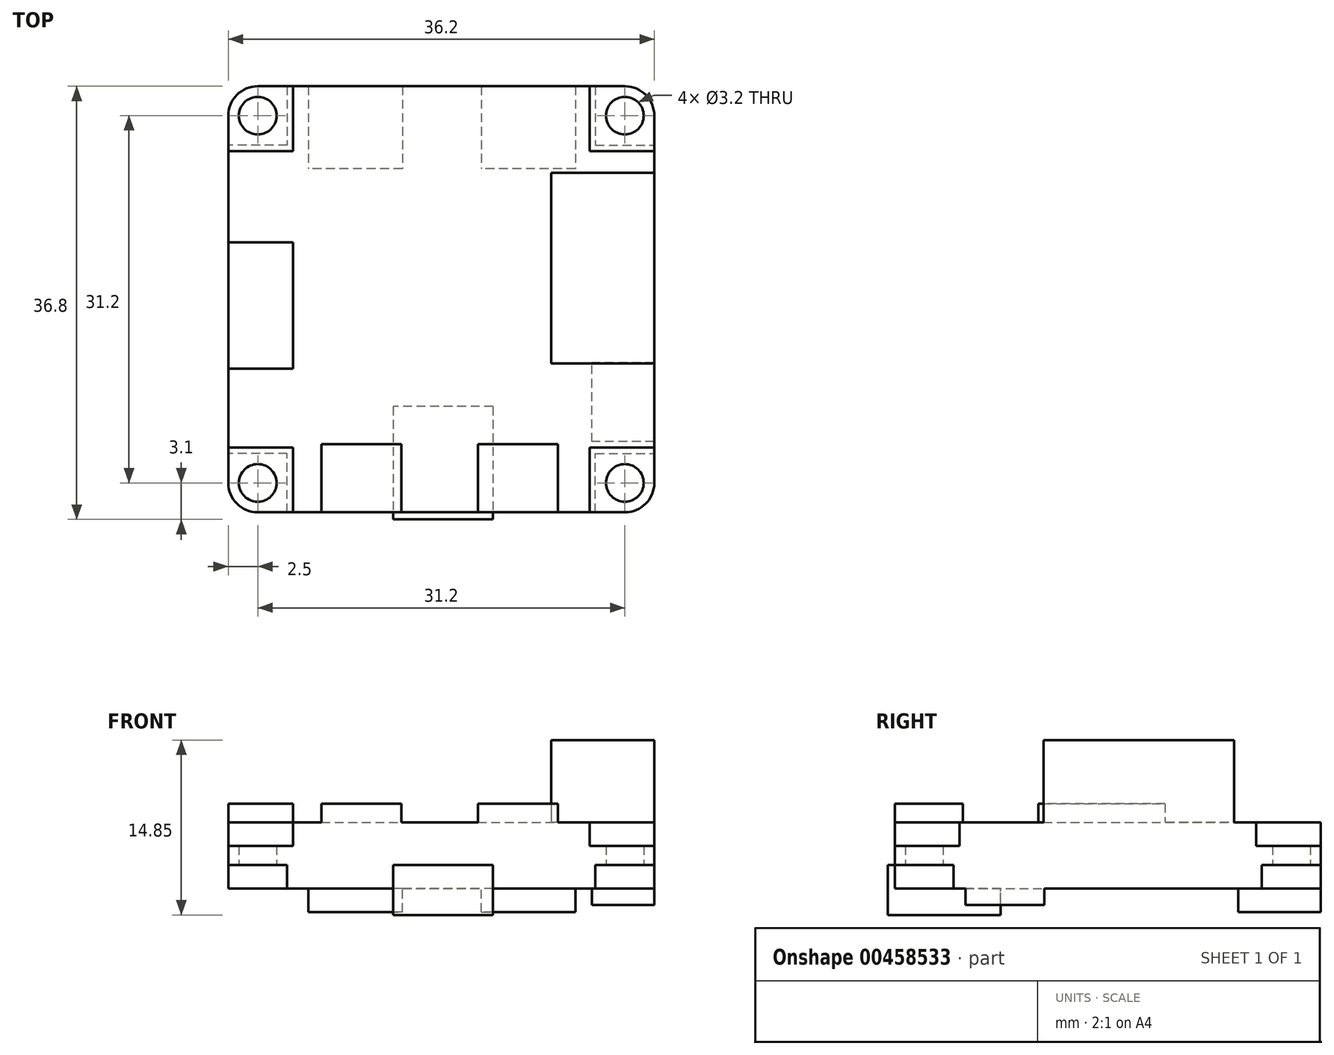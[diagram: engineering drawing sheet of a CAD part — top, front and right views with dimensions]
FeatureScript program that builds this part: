
annotation { "Feature Type Name" : "Feature", "Feature Type Description" : "" }
export const myFeature = defineFeature(function(context is Context, id is Id, definition is map)
    precondition{}
    {
        {
            var Q0;
            Q0=qCreatedBy(makeId("Top.planeOp"),FACE);
            var sketch = newSketch(context, id + "F0", { "sketchPlane" : qUnion([Q0])});
            skLineSegment(sketch, "E0.bottom", {"start": v(-15.6, 18.1) * mm, "end": v(15.6, 18.1) * mm});
            skLineSegment(sketch, "E0.top", {"start": v(-15.6, -18.1) * mm, "end": v(15.6, -18.1) * mm});
            skLineSegment(sketch, "E0.left", {"start": v(-18.1, 15.6) * mm, "end": v(-18.1, -15.6) * mm});
            skLineSegment(sketch, "E0.right", {"start": v(18.1, 15.6) * mm, "end": v(18.1, -15.6) * mm});
            skPoint(sketch, "E0.middle", {"position": v(0, 0) * mm});
            skPoint(sketch, "E1.visualSharp", {"position": v(-18.1, 18.1) * mm});
            skArc(sketch, "E1.filletArc", {"start": v(-15.6, 18.1) * mm, "mid": v(-17.37, 17.37) * mm, "end": v(-18.1, 15.6) * mm});
            skPoint(sketch, "E2.visualSharp", {"position": v(18.1, 18.1) * mm});
            skArc(sketch, "E2.filletArc", {"start": v(18.1, 15.6) * mm, "mid": v(17.37, 17.37) * mm, "end": v(15.6, 18.1) * mm});
            skPoint(sketch, "E3.visualSharp", {"position": v(18.1, -18.1) * mm});
            skArc(sketch, "E3.filletArc", {"start": v(15.6, -18.1) * mm, "mid": v(17.37, -17.37) * mm, "end": v(18.1, -15.6) * mm});
            skPoint(sketch, "E4.visualSharp", {"position": v(-18.1, -18.1) * mm});
            skArc(sketch, "E4.filletArc", {"start": v(-18.1, -15.6) * mm, "mid": v(-17.37, -17.37) * mm, "end": v(-15.6, -18.1) * mm});
            skCircle(sketch, "E5", {"center": v(-15.6, 15.6) * mm, "radius": 1.6 * mm});
            skCircle(sketch, "E6.MirrorC", {"center": v(15.6, 15.6) * mm, "radius": 1.6 * mm});
            skCircle(sketch, "E7.MirrorC", {"center": v(15.6, -15.6) * mm, "radius": 1.6 * mm});
            skCircle(sketch, "E8.MirrorC", {"center": v(-15.6, -15.6) * mm, "radius": 1.6 * mm});
            skSolve(sketch);
        }
        {
            var Q0;
            Q0=qSketchRegion(id+"F0",true);
            extrude(context, id + "F1", {"entities" : qUnion([Q0]), "depth" : 1.6 * mm});
        }
        {
            var Q0;
            Q0=makeQuery(id+"F1.opExtrude","CAP_FACE",FACE,{"disambiguationData":[OSD([sQuery(id+"F0.wireOp",EDGE,"E0.bottom"),sQuery(id+"F0.wireOp",EDGE,"E0.top"),sQuery(id+"F0.wireOp",EDGE,"E0.left"),sQuery(id+"F0.wireOp",EDGE,"E0.right"),sQuery(id+"F0.wireOp",EDGE,"E1.filletArc"),sQuery(id+"F0.wireOp",EDGE,"E2.filletArc"),sQuery(id+"F0.wireOp",EDGE,"E3.filletArc"),sQuery(id+"F0.wireOp",EDGE,"E4.filletArc"),sQuery(id+"F0.wireOp",EDGE,"E5"),sQuery(id+"F0.wireOp",EDGE,"E6.MirrorC"),sQuery(id+"F0.wireOp",EDGE,"E7.MirrorC"),sQuery(id+"F0.wireOp",EDGE,"E8.MirrorC")])],"isStart":false});
            var sketch = newSketch(context, id + "F2", { "sketchPlane" : qUnion([Q0])});
            skLineSegment(sketch, "E9.bottom", {"start": v(-18.1, -5.9) * mm, "end": v(-12.6, -5.9) * mm});
            skLineSegment(sketch, "E9.top", {"start": v(-18.1, 4.85) * mm, "end": v(-12.6, 4.85) * mm});
            skLineSegment(sketch, "E9.left", {"start": v(-18.1, -5.9) * mm, "end": v(-18.1, 4.85) * mm});
            skLineSegment(sketch, "E9.right", {"start": v(-12.6, -5.9) * mm, "end": v(-12.6, 4.85) * mm});
            skLineSegment(sketch, "E10.bottom", {"start": v(-10.2, -18.1) * mm, "end": v(-3.4, -18.1) * mm});
            skLineSegment(sketch, "E10.top", {"start": v(-10.2, -12.3) * mm, "end": v(-3.4, -12.3) * mm});
            skLineSegment(sketch, "E10.left", {"start": v(-10.2, -18.1) * mm, "end": v(-10.2, -12.3) * mm});
            skLineSegment(sketch, "E10.right", {"start": v(-3.4, -18.1) * mm, "end": v(-3.4, -12.3) * mm});
            skLineSegment(sketch, "E11.bottom", {"start": v(3.1, -18.1) * mm, "end": v(9.9, -18.1) * mm});
            skLineSegment(sketch, "E11.top", {"start": v(3.1, -12.3) * mm, "end": v(9.9, -12.3) * mm});
            skLineSegment(sketch, "E11.left", {"start": v(3.1, -18.1) * mm, "end": v(3.1, -12.3) * mm});
            skLineSegment(sketch, "E11.right", {"start": v(9.9, -18.1) * mm, "end": v(9.9, -12.3) * mm});
            skLineSegment(sketch, "E12.bottom", {"start": v(18.1, -5.46) * mm, "end": v(9.35, -5.46) * mm});
            skLineSegment(sketch, "E12.top", {"start": v(18.1, 10.74) * mm, "end": v(9.35, 10.74) * mm});
            skLineSegment(sketch, "E12.left", {"start": v(18.1, -5.46) * mm, "end": v(18.1, 10.74) * mm});
            skLineSegment(sketch, "E12.right", {"start": v(9.35, -5.46) * mm, "end": v(9.35, 10.74) * mm});
            skLineSegment(sketch, "E13", {"start": v(-18.1, -12.6) * mm, "end": v(-12.6, -12.6) * mm});
            skLineSegment(sketch, "E14", {"start": v(-12.6, -12.6) * mm, "end": v(-12.6, -18.1) * mm});
            skLineSegment(sketch, "E15.MirrorCS", {"start": v(-18.1, 12.6) * mm, "end": v(-12.6, 12.6) * mm});
            skLineSegment(sketch, "E16.MirrorCS", {"start": v(-12.6, 12.6) * mm, "end": v(-12.6, 18.1) * mm});
            skLineSegment(sketch, "E17.MirrorCS", {"start": v(12.6, 12.6) * mm, "end": v(12.6, 18.1) * mm});
            skLineSegment(sketch, "E18.MirrorCS", {"start": v(18.1, 12.6) * mm, "end": v(12.6, 12.6) * mm});
            skLineSegment(sketch, "E19.MirrorCS", {"start": v(12.6, -12.6) * mm, "end": v(12.6, -18.1) * mm});
            skLineSegment(sketch, "E20.MirrorCS", {"start": v(18.1, -12.6) * mm, "end": v(12.6, -12.6) * mm});
            skSolve(sketch);
        }
        {
            var Q0;
            Q0=makeQuery(id+"F2.imprint","IMPRINT",FACE,{"disambiguationData":[TD([[makeQuery(id+"F2.imprint","IMPRINT",EDGE,{"derivedFrom":sQuery(id+"F2.wireOp",EDGE,"E9.bottom")}),1.0]])]});
            var Q1;
            Q1=makeQuery(id+"F2.imprint","IMPRINT",FACE,{"disambiguationData":[TD([[makeQuery(id+"F2.imprint","IMPRINT",EDGE,{"derivedFrom":sQuery(id+"F2.wireOp",EDGE,"E10.bottom")}),1.0]])]});
            var Q2;
            Q2=makeQuery(id+"F2.imprint","IMPRINT",FACE,{"disambiguationData":[TD([[makeQuery(id+"F2.imprint","IMPRINT",EDGE,{"derivedFrom":sQuery(id+"F2.wireOp",EDGE,"E11.bottom")}),1.0]])]});
            extrude(context, id + "F3", {"entities" : qUnion([Q0, Q1, Q2]), "operationType" : NewBodyOperationType.ADD, "depth" : 3.6 * mm});
        }
        {
            var Q0;
            Q0=makeQuery(id+"F2.imprint","IMPRINT",FACE,{"disambiguationData":[TD([[makeQuery(id+"F2.imprint","IMPRINT",EDGE,{"derivedFrom":sQuery(id+"F2.wireOp",EDGE,"E12.bottom")}),-1.0]])]});
            extrude(context, id + "F4", {"entities" : qUnion([Q0]), "operationType" : NewBodyOperationType.ADD, "depth" : 9 * mm});
        }
        {
            var Q0;
            {var subQ14=sQuery(id+"F2.wireOp",EDGE,"E9.bottom");Q0=makeQuery(id+"F2.imprint","IMPRINT",FACE,{"disambiguationData":[TD([[makeQuery(id+"F2.imprint","IMPRINT",EDGE,{"derivedFrom":subQ14}),-1.0]])]});}
            extrude(context, id + "F5", {"entities" : qUnion([Q0]), "operationType" : NewBodyOperationType.ADD, "depth" : 2 * mm});
        }
        {
            var Q0;
            Q0=makeQuery(id+"F1.opExtrude","CAP_FACE",FACE,{"disambiguationData":[OSD([sQuery(id+"F0.wireOp",EDGE,"E0.bottom"),sQuery(id+"F0.wireOp",EDGE,"E0.top"),sQuery(id+"F0.wireOp",EDGE,"E0.left"),sQuery(id+"F0.wireOp",EDGE,"E0.right"),sQuery(id+"F0.wireOp",EDGE,"E1.filletArc"),sQuery(id+"F0.wireOp",EDGE,"E2.filletArc"),sQuery(id+"F0.wireOp",EDGE,"E3.filletArc"),sQuery(id+"F0.wireOp",EDGE,"E4.filletArc"),sQuery(id+"F0.wireOp",EDGE,"E5"),sQuery(id+"F0.wireOp",EDGE,"E6.MirrorC"),sQuery(id+"F0.wireOp",EDGE,"E7.MirrorC"),sQuery(id+"F0.wireOp",EDGE,"E8.MirrorC")])],"isStart":true});
            var sketch = newSketch(context, id + "F6", { "sketchPlane" : qUnion([Q0])});
            skLineSegment(sketch, "E21.bottom", {"start": v(18.1, 12.1) * mm, "end": v(12.8, 12.1) * mm});
            skLineSegment(sketch, "E21.top", {"start": v(18.1, 5.4) * mm, "end": v(12.8, 5.4) * mm});
            skLineSegment(sketch, "E21.left", {"start": v(18.1, 12.1) * mm, "end": v(18.1, 5.4) * mm});
            skLineSegment(sketch, "E21.right", {"start": v(12.8, 12.1) * mm, "end": v(12.8, 5.4) * mm});
            skLineSegment(sketch, "E22.bottom", {"start": v(11.4, -18.1) * mm, "end": v(3.4, -18.1) * mm});
            skLineSegment(sketch, "E22.top", {"start": v(11.4, -11.1) * mm, "end": v(3.4, -11.1) * mm});
            skLineSegment(sketch, "E22.left", {"start": v(11.4, -18.1) * mm, "end": v(11.4, -11.1) * mm});
            skLineSegment(sketch, "E22.right", {"start": v(3.4, -18.1) * mm, "end": v(3.4, -11.1) * mm});
            skLineSegment(sketch, "E23.bottom", {"start": v(-3.3, -18.1) * mm, "end": v(-11.3, -18.1) * mm});
            skLineSegment(sketch, "E23.top", {"start": v(-3.3, -11.1) * mm, "end": v(-11.3, -11.1) * mm});
            skLineSegment(sketch, "E23.left", {"start": v(-3.3, -18.1) * mm, "end": v(-3.3, -11.1) * mm});
            skLineSegment(sketch, "E23.right", {"start": v(-11.3, -18.1) * mm, "end": v(-11.3, -11.1) * mm});
            skLineSegment(sketch, "E24.bottom", {"start": v(4.4, 9.1) * mm, "end": v(-4.1, 9.1) * mm});
            skLineSegment(sketch, "E24.top", {"start": v(4.4, 18.7) * mm, "end": v(-4.1, 18.7) * mm});
            skLineSegment(sketch, "E24.left", {"start": v(4.4, 9.1) * mm, "end": v(4.4, 18.7) * mm});
            skLineSegment(sketch, "E24.right", {"start": v(-4.1, 9.1) * mm, "end": v(-4.1, 18.7) * mm});
            skLineSegment(sketch, "E25", {"start": v(-13.1, -18.1) * mm, "end": v(-13.1, -13.1) * mm});
            skLineSegment(sketch, "E26", {"start": v(-13.1, -13.1) * mm, "end": v(-18.1, -13.1) * mm});
            skLineSegment(sketch, "E27.MirrorCS", {"start": v(13.1, -13.1) * mm, "end": v(18.1, -13.1) * mm});
            skLineSegment(sketch, "E28.MirrorCS", {"start": v(13.1, -18.1) * mm, "end": v(13.1, -13.1) * mm});
            skLineSegment(sketch, "E29.MirrorCS", {"start": v(13.1, 13.1) * mm, "end": v(18.1, 13.1) * mm});
            skLineSegment(sketch, "E30.MirrorCS", {"start": v(13.1, 18.1) * mm, "end": v(13.1, 13.1) * mm});
            skLineSegment(sketch, "E31.MirrorCS", {"start": v(-13.1, 13.1) * mm, "end": v(-18.1, 13.1) * mm});
            skLineSegment(sketch, "E32.MirrorCS", {"start": v(-13.1, 18.1) * mm, "end": v(-13.1, 13.1) * mm});
            skSolve(sketch);
        }
        {
            var Q0;
            {var subQ23=sQuery(id+"F6.wireOp",EDGE,"E21.bottom");Q0=makeQuery(id+"F6.imprint","IMPRINT",FACE,{"disambiguationData":[TD([[makeQuery(id+"F6.imprint","IMPRINT",EDGE,{"derivedFrom":subQ23}),-1.0]])]});}
            extrude(context, id + "F7", {"entities" : qUnion([Q0]), "operationType" : NewBodyOperationType.ADD, "depth" : 2 * mm});
        }
        {
            var Q0;
            {var subQ0=sQuery(id+"F6.wireOp",EDGE,"E24.top");Q0=makeQuery(id+"F6.imprint","IMPRINT",FACE,{"disambiguationData":[TD([[makeQuery(id+"F6.imprint","IMPRINT",EDGE,{"derivedFrom":subQ0}),1.0]])]});}
            var Q1;
            {var subQ0=sQuery(id+"F6.wireOp",EDGE,"E24.bottom");Q1=makeQuery(id+"F6.imprint","IMPRINT",FACE,{"disambiguationData":[TD([[makeQuery(id+"F6.imprint","IMPRINT",EDGE,{"derivedFrom":subQ0}),-1.0]])]});}
            extrude(context, id + "F8", {"entities" : qUnion([Q0, Q1]), "operationType" : NewBodyOperationType.ADD, "depth" : 4.25 * mm});
        }
        {
            var Q0;
            Q0=makeQuery(id+"F6.imprint","IMPRINT",FACE,{"disambiguationData":[TD([[makeQuery(id+"F6.imprint","IMPRINT",EDGE,{"derivedFrom":sQuery(id+"F6.wireOp",EDGE,"E21.bottom")}),1.0]])]});
            extrude(context, id + "F9", {"entities" : qUnion([Q0]), "operationType" : NewBodyOperationType.ADD, "depth" : 3.4 * mm});
        }
        {
            var Q0;
            Q0=makeQuery(id+"F6.imprint","IMPRINT",FACE,{"disambiguationData":[TD([[makeQuery(id+"F6.imprint","IMPRINT",EDGE,{"derivedFrom":sQuery(id+"F6.wireOp",EDGE,"E22.bottom")}),1.0]])]});
            var Q1;
            Q1=makeQuery(id+"F6.imprint","IMPRINT",FACE,{"disambiguationData":[TD([[makeQuery(id+"F6.imprint","IMPRINT",EDGE,{"derivedFrom":sQuery(id+"F6.wireOp",EDGE,"E23.bottom")}),1.0]])]});
            extrude(context, id + "F10", {"entities" : qUnion([Q0, Q1]), "operationType" : NewBodyOperationType.ADD, "depth" : 4 * mm});
        }
    });
